MODEL noise_test
KIND model
BLOCK [Reference] Band-Limited\nWhite Noise1  REF=simulink/Sources/Band-Limited\nWhite Noise
  Cov = 0.05
  Ports = [0, 1]
  SID = 1
  SourceBlock = simulink/Sources/Band-Limited\nWhite Noise
  SourceType = Band-Limited White Noise.
  Ts = 0.001
  VectorParams1D = on
  seed = [23341]
BLOCK [Scope] Scope
  DataFormat = StructureWithTime
  Floating = off
  NumInputPorts = 1
  Ports = [1]
  SID = 3
  SampleTime = 0
  ShowLegends = off
  ZoomMode = yonly
BLOCK [TransferFcn] Transfer Fcn
  Denominator = [50 1]
  Numerator = [0.5]
  SID = 7
ANNOTATION (root): 
LINE Band-Limited\nWhite Noise1:1 -> Transfer Fcn:1
LINE Transfer Fcn:1 -> Scope:1
